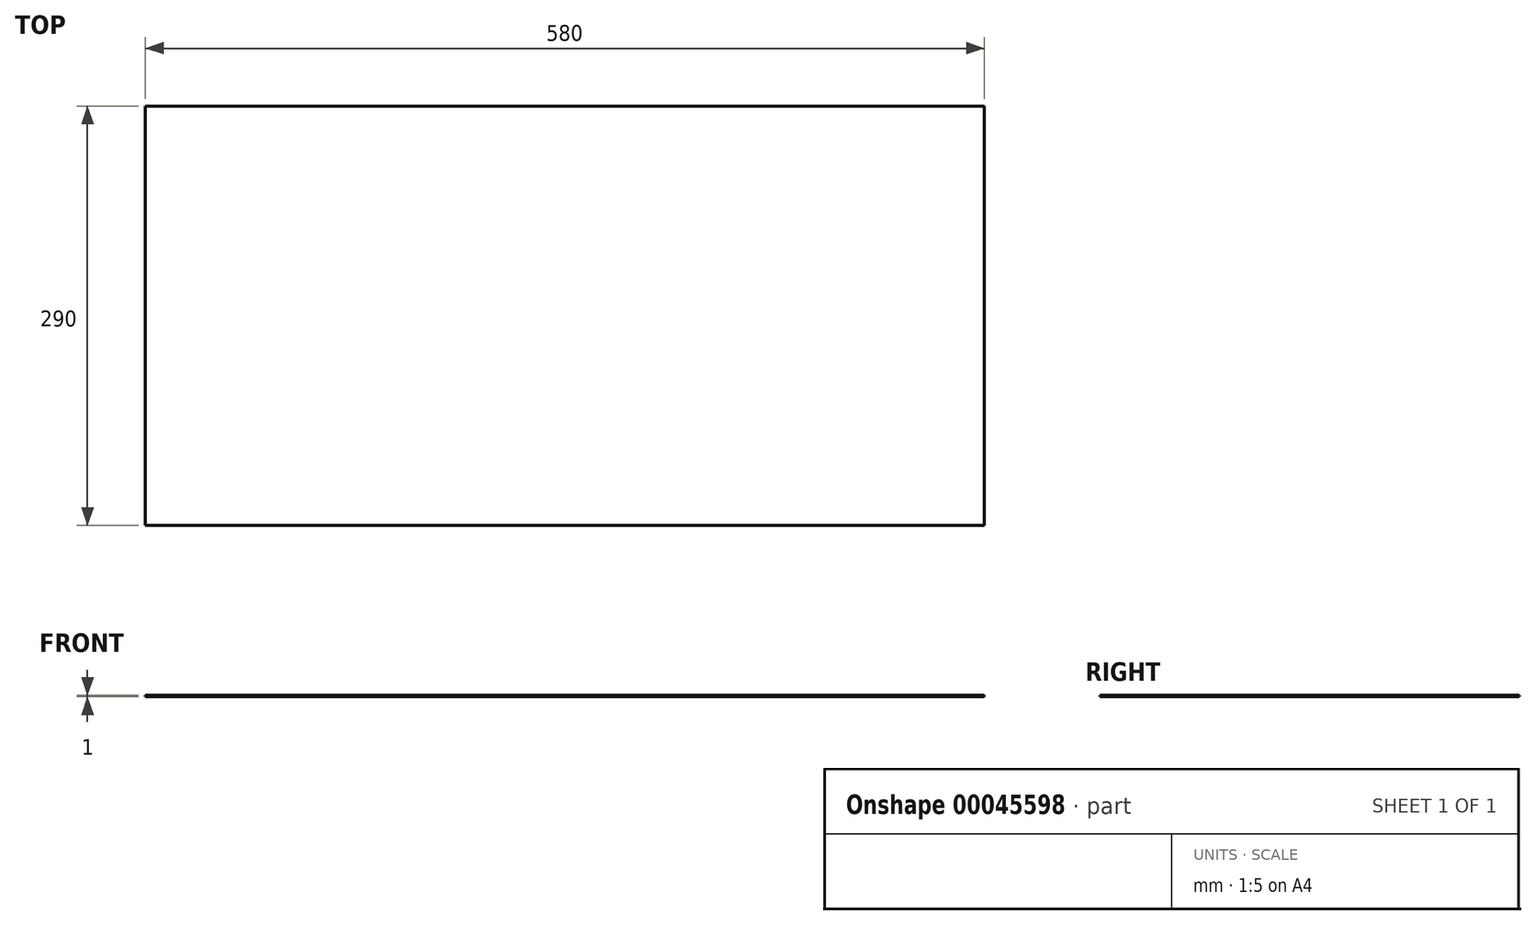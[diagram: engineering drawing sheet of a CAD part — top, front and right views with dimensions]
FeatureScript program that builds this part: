
annotation { "Feature Type Name" : "Feature", "Feature Type Description" : "" }
export const myFeature = defineFeature(function(context is Context, id is Id, definition is map)
    precondition{}
    {
        {
            var Q0;
            Q0=qCreatedBy(makeId("Top.planeOp"),FACE);
            var sketch = newSketch(context, id + "F0", { "sketchPlane" : qUnion([Q0])});
            skLineSegment(sketch, "E0.bottom", {"start": v(0, 0) * mm, "end": v(580, 0) * mm});
            skLineSegment(sketch, "E0.top", {"start": v(0, 290) * mm, "end": v(580, 290) * mm});
            skLineSegment(sketch, "E0.left", {"start": v(0, 0) * mm, "end": v(0, 290) * mm});
            skLineSegment(sketch, "E0.right", {"start": v(580, 0) * mm, "end": v(580, 290) * mm});
            skSolve(sketch);
        }
        {
            var Q0;
            Q0=makeQuery(id+"F0.imprint","IMPRINT",FACE,{"disambiguationData":[TD([[makeQuery(id+"F0.imprint","IMPRINT",EDGE,{"derivedFrom":sQuery(id+"F0.wireOp",EDGE,"E0.bottom")}),1.0]])]});
            extrude(context, id + "F1", {"entities" : qUnion([Q0]), "depth" : 1 * mm});
        }
    });
